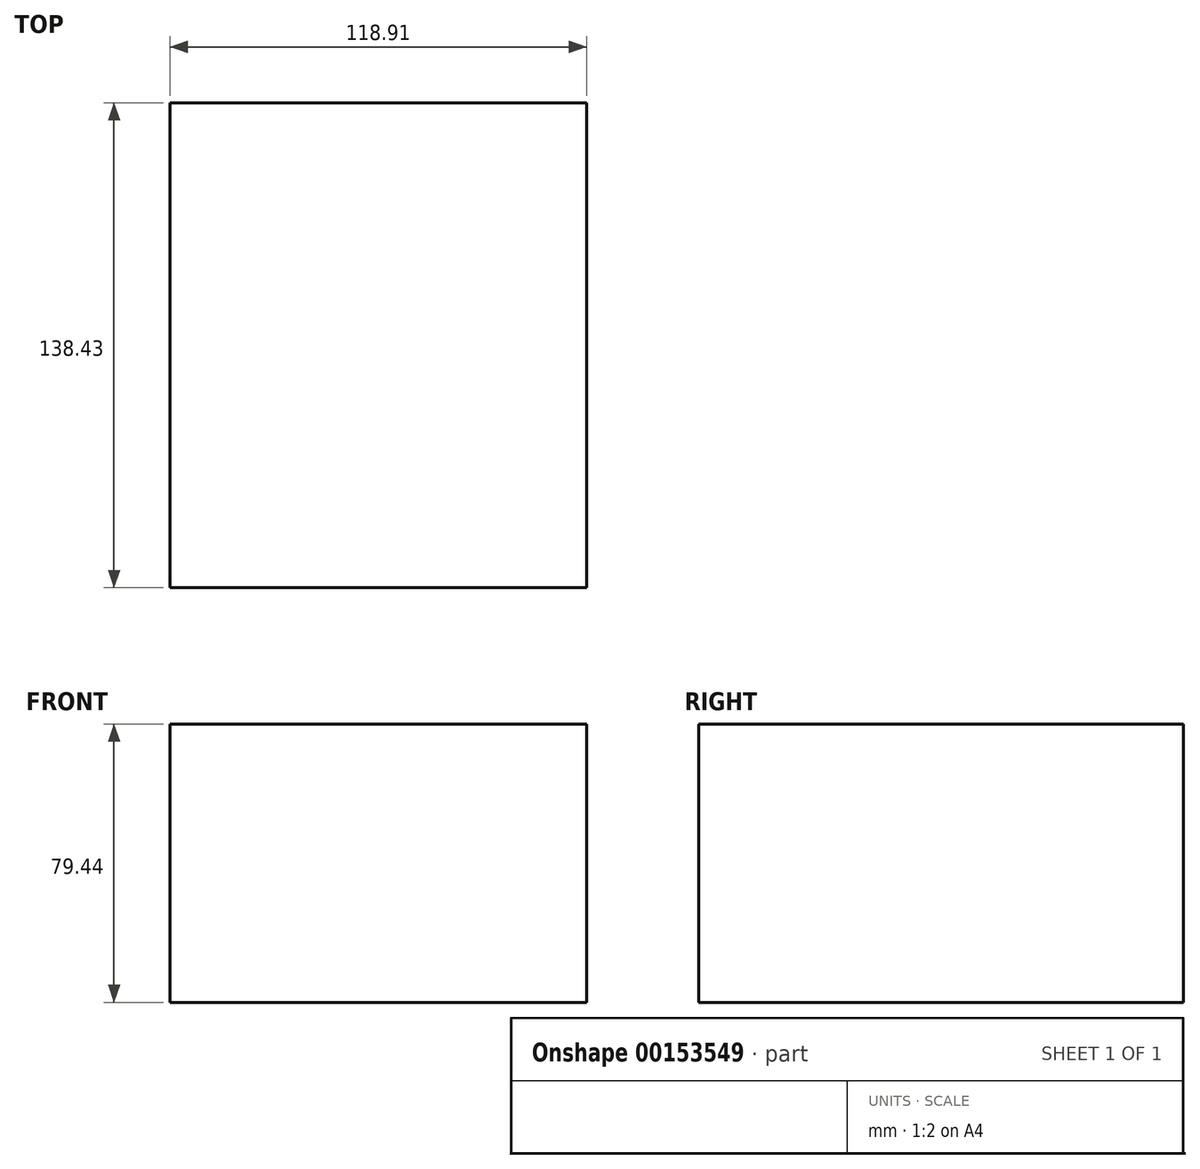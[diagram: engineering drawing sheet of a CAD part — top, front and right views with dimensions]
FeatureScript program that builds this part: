
annotation { "Feature Type Name" : "Feature", "Feature Type Description" : "" }
export const myFeature = defineFeature(function(context is Context, id is Id, definition is map)
    precondition{}
    {
        {
            var Q0;
            Q0=qCreatedBy(makeId("Front.planeOp"),FACE);
            var sketch = newSketch(context, id + "F0", { "sketchPlane" : qUnion([Q0])});
            skLineSegment(sketch, "E0.bottom", {"start": v(33.27, 44.88) * mm, "end": v(-85.64, 44.88) * mm});
            skLineSegment(sketch, "E0.top", {"start": v(33.27, -34.56) * mm, "end": v(-85.64, -34.56) * mm});
            skLineSegment(sketch, "E0.left", {"start": v(33.27, 44.88) * mm, "end": v(33.27, -34.56) * mm});
            skLineSegment(sketch, "E0.right", {"start": v(-85.64, 44.88) * mm, "end": v(-85.64, -34.56) * mm});
            skSolve(sketch);
        }
        {
            var Q0;
            Q0=makeQuery(id+"F0.imprint","IMPRINT",FACE,{"disambiguationData":[TD([[makeQuery(id+"F0.imprint","IMPRINT",EDGE,{"derivedFrom":sQuery(id+"F0.wireOp",EDGE,"E0.bottom")}),1.0]])]});
            extrude(context, id + "F1", {"entities" : qUnion([Q0]), "depth" : 138.43 * mm});
        }
    });
